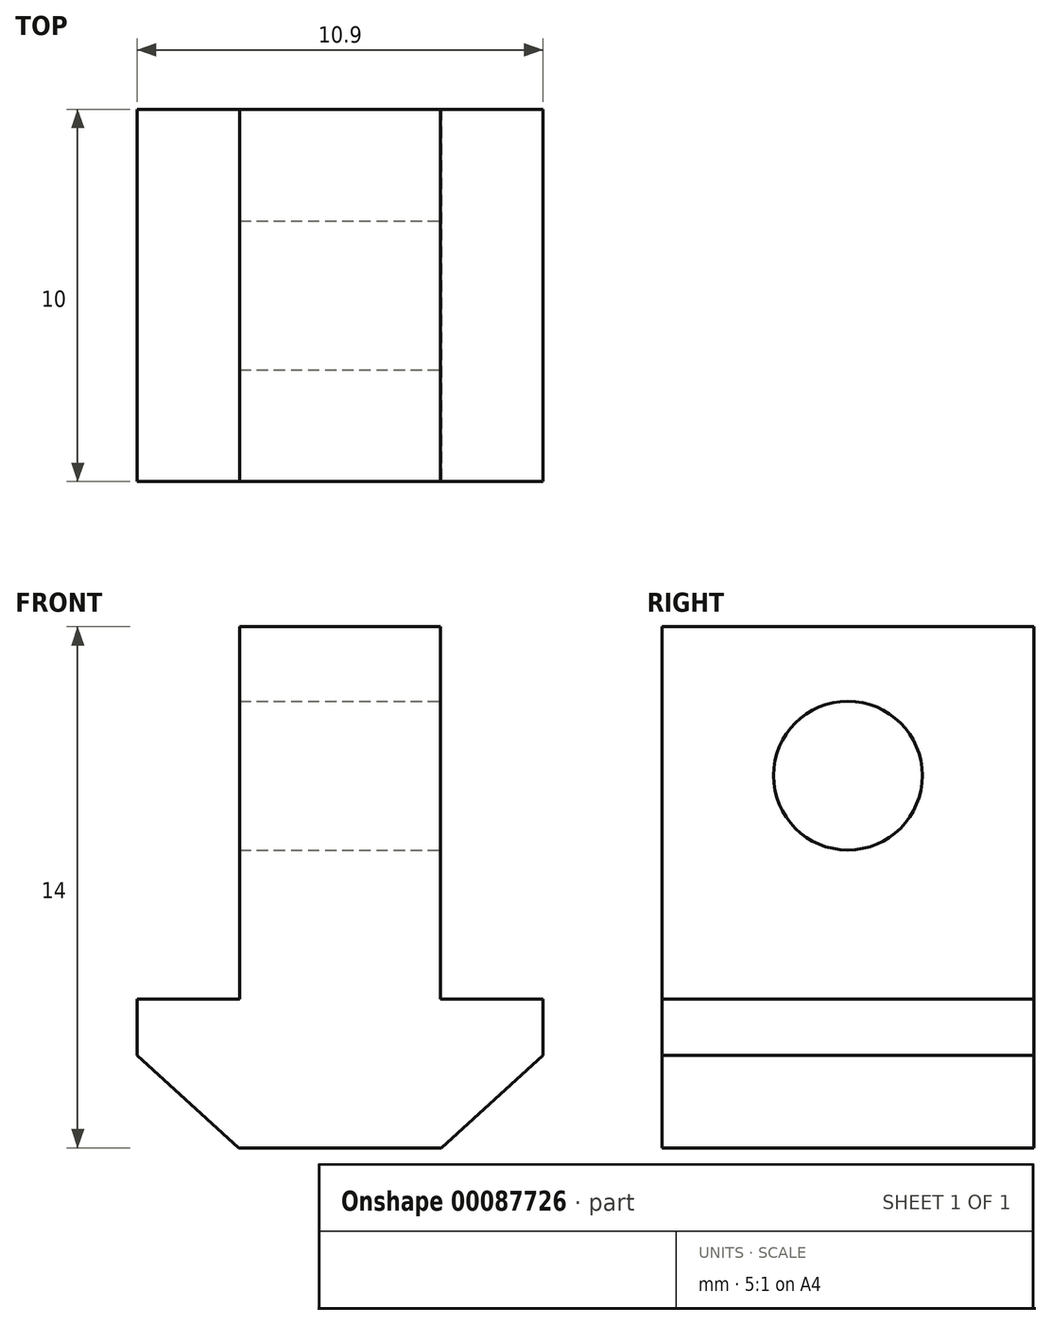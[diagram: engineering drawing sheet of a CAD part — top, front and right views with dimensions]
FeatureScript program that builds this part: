
annotation { "Feature Type Name" : "Feature", "Feature Type Description" : "" }
export const myFeature = defineFeature(function(context is Context, id is Id, definition is map)
    precondition{}
    {
        {
            var Q0;
            Q0=qCreatedBy(makeId("Right.planeOp"),FACE);
            var sketch = newSketch(context, id + "F0", { "sketchPlane" : qUnion([Q0])});
            skLineSegment(sketch, "E0.bottom", {"start": v(0, 0) * mm, "end": v(10, 0) * mm});
            skLineSegment(sketch, "E0.top", {"start": v(0, 6.1) * mm, "end": v(10, 6.1) * mm});
            skLineSegment(sketch, "E0.left", {"start": v(0, 0) * mm, "end": v(0, 6.1) * mm});
            skLineSegment(sketch, "E0.right", {"start": v(10, 0) * mm, "end": v(10, 6.1) * mm});
            skSolve(sketch);
        }
        {
            var Q0;
            Q0=makeQuery(id+"F0.imprint","IMPRINT",FACE,{"disambiguationData":[TD([[makeQuery(id+"F0.imprint","IMPRINT",EDGE,{"derivedFrom":sQuery(id+"F0.wireOp",EDGE,"E0.bottom")}),1.0]])]});
            extrude(context, id + "F1", {"entities" : qUnion([Q0]), "depth" : 10.9 * mm});
        }
        {
            var Q0;
            Q0=makeQuery(id+"F1.opExtrude","SWEPT_FACE",FACE,{"disambiguationData":[OSD([sQuery(id+"F0.wireOp",EDGE,"E0.left")])]});
            var sketch = newSketch(context, id + "F2", { "sketchPlane" : qUnion([Q0])});
            skLineSegment(sketch, "E1.bottom", {"start": v(10.9, 0) * mm, "end": v(0, 0) * mm});
            skLineSegment(sketch, "E1.top", {"start": v(10.9, 4) * mm, "end": v(0, 4) * mm});
            skLineSegment(sketch, "E1.left", {"start": v(10.9, 0) * mm, "end": v(10.9, 4) * mm});
            skLineSegment(sketch, "E1.right", {"start": v(0, 0) * mm, "end": v(0, 4) * mm});
            skLineSegment(sketch, "E2", {"start": v(5.45, 0) * mm, "end": v(8.18, 0) * mm});
            skLineSegment(sketch, "E3", {"start": v(5.45, 0) * mm, "end": v(2.72, 0) * mm});
            skLineSegment(sketch, "E4", {"start": v(0, 4) * mm, "end": v(0, 2.48) * mm});
            skLineSegment(sketch, "E5", {"start": v(0, 2.48) * mm, "end": v(2.72, 0) * mm});
            skLineSegment(sketch, "E6", {"start": v(10.9, 4) * mm, "end": v(10.9, 2.48) * mm});
            skLineSegment(sketch, "E7", {"start": v(10.9, 2.48) * mm, "end": v(8.18, 0) * mm});
            skLineSegment(sketch, "E8", {"start": v(2.72, 0) * mm, "end": v(2.72, 2.48) * mm});
            skSolve(sketch);
        }
        {
            var Q0;
            {var subQ0=sQuery(id+"F2.wireOp",EDGE,"E1.top");Q0=makeQuery(id+"F2.imprint","IMPRINT",FACE,{"disambiguationData":[TD([[makeQuery(id+"F2.imprint","IMPRINT",EDGE,{"derivedFrom":subQ0}),-1.0]])]});}
            var Q1;
            {var subQ0=sQuery(id+"F2.wireOp",EDGE,"E1.right");Q1=makeQuery(id+"F2.imprint","IMPRINT",FACE,{"disambiguationData":[TD([[makeQuery(id+"F2.imprint","IMPRINT",EDGE,{"derivedFrom":subQ0}),-1.0]])]});}
            var Q2;
            {var subQ0=sQuery(id+"F2.wireOp",EDGE,"E1.left");Q2=makeQuery(id+"F2.imprint","IMPRINT",FACE,{"disambiguationData":[TD([[makeQuery(id+"F2.imprint","IMPRINT",EDGE,{"derivedFrom":subQ0}),1.0]])]});}
            extrude(context, id + "F3", {"entities" : qUnion([Q0, Q1, Q2]), "operationType" : NewBodyOperationType.REMOVE, "oppositeDirection" : true, "depth" : 25 * mm});
        }
        {
            var Q0;
            Q0=makeQuery(id+"F3.boolean.opBoolean","COPY",FACE,{"derivedFrom":makeQuery(id+"F3.opExtrude","SWEPT_FACE",FACE,{"disambiguationData":[OSD([sQuery(id+"F2.wireOp",EDGE,"E1.top")])]})});
            var sketch = newSketch(context, id + "F4", { "sketchPlane" : qUnion([Q0])});
            skLineSegment(sketch, "E9", {"start": v(5.45, 10) * mm, "end": v(8.15, 10) * mm});
            skLineSegment(sketch, "E10", {"start": v(5.45, 10) * mm, "end": v(2.75, 10) * mm});
            skLineSegment(sketch, "E11", {"start": v(2.75, 10) * mm, "end": v(2.75, 0) * mm});
            skLineSegment(sketch, "E12", {"start": v(2.75, 0) * mm, "end": v(8.15, 0) * mm});
            skLineSegment(sketch, "E13", {"start": v(8.15, 0) * mm, "end": v(8.15, 10) * mm});
            skSolve(sketch);
        }
        {
            var Q0;
            Q0=makeQuery(id+"F4.imprint","IMPRINT",FACE,{"disambiguationData":[TD([[makeQuery(id+"F4.imprint","IMPRINT",EDGE,{"derivedFrom":sQuery(id+"F4.wireOp",EDGE,"E9")}),1.0]])]});
            extrude(context, id + "F5", {"entities" : qUnion([Q0]), "operationType" : NewBodyOperationType.ADD, "depth" : 12 * mm});
        }
        {
            var Q0;
            Q0=makeQuery(id+"F5.opExtrude","SWEPT_FACE",FACE,{"disambiguationData":[OSD([sQuery(id+"F4.wireOp",EDGE,"E13")])]});
            var sketch = newSketch(context, id + "F6", { "sketchPlane" : qUnion([Q0])});
            skLineSegment(sketch, "E14", {"start": v(10, 10) * mm, "end": v(0, 10) * mm});
            skCircle(sketch, "E15", {"center": v(5, 10) * mm, "radius": 2 * mm});
            skLineSegment(sketch, "E16.bottom", {"start": v(10, 16) * mm, "end": v(0, 16) * mm});
            skLineSegment(sketch, "E16.top", {"start": v(10, 14) * mm, "end": v(0, 14) * mm});
            skLineSegment(sketch, "E16.left", {"start": v(10, 16) * mm, "end": v(10, 14) * mm});
            skLineSegment(sketch, "E16.right", {"start": v(0, 16) * mm, "end": v(0, 14) * mm});
            skSolve(sketch);
        }
        {
            var Q0;
            {var subQ0=sQuery(id+"F6.wireOp",EDGE,"E15");var subQ1=sQuery(id+"F6.wireOp",EDGE,"E14");var subQ2=makeQuery(id+"F6.imprint","INTERSECT",VERTEX,{"disambiguationData":[OD(0.0)],"derivedFrom":[subQ1,subQ0]});Q0=makeQuery(id+"F6.imprint","IMPRINT",FACE,{"disambiguationData":[TD([[makeQuery(id+"F6.imprint","IMPRINT",EDGE,{"disambiguationData":[TD([[subQ2,-1.0]])],"derivedFrom":subQ1}),-1.0]])]});}
            var Q1;
            {var subQ0=sQuery(id+"F6.wireOp",EDGE,"E15");var subQ1=sQuery(id+"F6.wireOp",EDGE,"E14");var subQ2=makeQuery(id+"F6.imprint","INTERSECT",VERTEX,{"disambiguationData":[OD(0.0)],"derivedFrom":[subQ1,subQ0]});Q1=makeQuery(id+"F6.imprint","IMPRINT",FACE,{"disambiguationData":[TD([[makeQuery(id+"F6.imprint","IMPRINT",EDGE,{"disambiguationData":[TD([[subQ2,-1.0]])],"derivedFrom":subQ1}),1.0]])]});}
            var Q2;
            Q2=makeQuery(id+"F6.imprint","IMPRINT",FACE,{"disambiguationData":[TD([[makeQuery(id+"F6.imprint","IMPRINT",EDGE,{"derivedFrom":sQuery(id+"F6.wireOp",EDGE,"E16.bottom")}),-1.0]])]});
            extrude(context, id + "F7", {"entities" : qUnion([Q0, Q1, Q2]), "operationType" : NewBodyOperationType.REMOVE, "oppositeDirection" : true, "depth" : 25 * mm});
        }
    });
